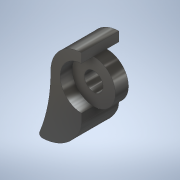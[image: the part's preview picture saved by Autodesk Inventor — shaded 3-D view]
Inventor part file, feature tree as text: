
AUTODESK INVENTOR PART (.ipt)
format: ipt  version: 2021 (Build 250183000, 183)  size: 168,960 bytes
history: native  units: in
note: dims shown in document units (in); Inventor stores cm internally (conversion verified against a paired STEP export)
features: extrude x4, sketch x4, projected_geometry x3, fillet x2, plane x1
ambient origin geometry x8: Origin, YZ Plane, XZ Plane, XY Plane, X Axis, Y Axis, Z Axis, Center Point
bodies: Solid1 (feature_tree)
feature tree (14):
  extrude  "Extrusion1"  Depth=0.0787in
  fillet  "Fillet1"  Radius=0.0787in
  extrude  "Extrusion2"  Depth=0.1575in TaperAngle=0.0deg
  extrude  "Extrusion3"  Depth=0.0512in TaperAngle=0.0deg
  plane  "Work Plane5"
  extrude  "Extrusion6"  Depth=0.0118in
  fillet  "Fillet2"  Radius=0.0187in
  sketch  "Sketch1"  dims[d0=0.3937in d1=0.1811in d2=0.0787in]
  sketch  "Sketch2"  dims[d3=0.2598in d4=0.1575in d5=0.0in]
  projected_geometry  "Projected Loop1"
  sketch  "Sketch3"  dims[d6=0.0787in d7=0.0512in d8=0.0in]
  projected_geometry  "Projected Loop2"
  sketch  "Sketch6"  dims[d9=0.0512in d10=0.0in d22=0.0217in d23=0.0187in d24=0.0in d25=0.0118in d26=0.0264in]
  projected_geometry  "Projected Loop4"
